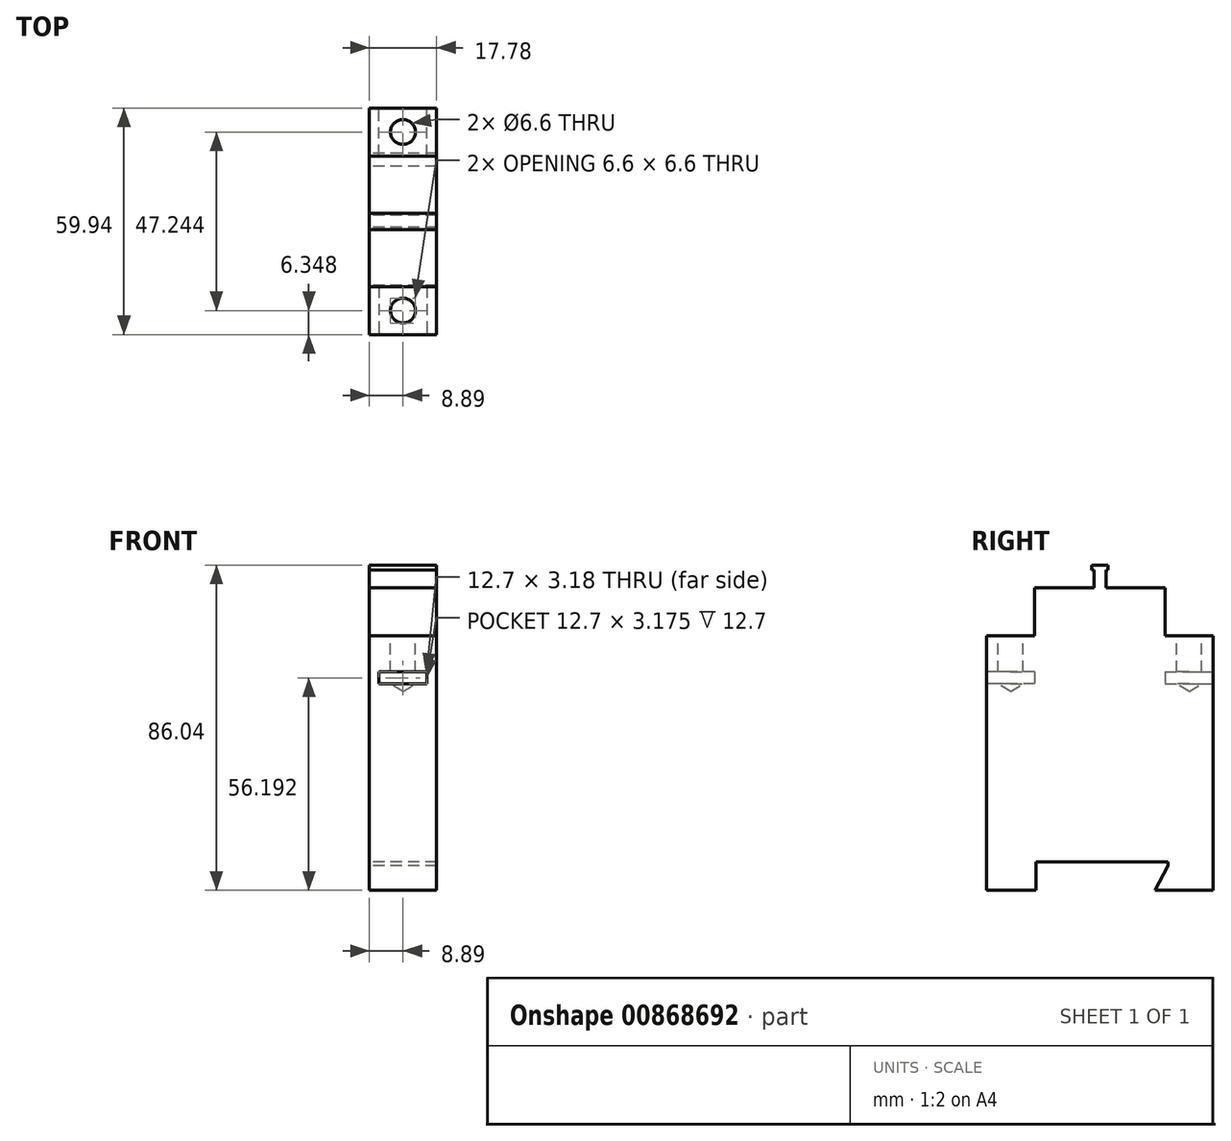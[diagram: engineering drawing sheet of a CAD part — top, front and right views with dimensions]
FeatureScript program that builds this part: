
annotation { "Feature Type Name" : "Feature", "Feature Type Description" : "" }
export const myFeature = defineFeature(function(context is Context, id is Id, definition is map)
    precondition{}
    {
        {
            var Q0;
            Q0=qCreatedBy(makeId("Right.planeOp"),FACE);
            var sketch = newSketch(context, id + "F0", { "sketchPlane" : qUnion([Q0])});
            skLineSegment(sketch, "E0.bottom", {"start": v(-17.8, 40) * mm, "end": v(16.74, 40) * mm});
            skLineSegment(sketch, "E0.top", {"start": v(-30.5, -40) * mm, "end": v(29.44, -40) * mm});
            skLineSegment(sketch, "E0.left", {"start": v(-30.5, 27.3) * mm, "end": v(-30.5, -40) * mm});
            skLineSegment(sketch, "E0.right", {"start": v(29.44, 27.3) * mm, "end": v(29.44, -40) * mm});
            skPoint(sketch, "E0.middle", {"position": v(0, 0) * mm});
            skLineSegment(sketch, "E1", {"start": v(-17.5, -33.5) * mm, "end": v(-17.5, -32.5) * mm});
            skLineSegment(sketch, "E2", {"start": v(-17.5, -32.5) * mm, "end": v(17.5, -32.5) * mm});
            skLineSegment(sketch, "E3", {"start": v(17.5, -32.5) * mm, "end": v(17.5, -33.5) * mm});
            skPoint(sketch, "E4.orphan", {"position": v(-17.5, -40) * mm});
            skLineSegment(sketch, "E5", {"start": v(-17.5, -33.5) * mm, "end": v(-17.5, -40) * mm});
            skLineSegment(sketch, "E6", {"start": v(17.5, -33.5) * mm, "end": v(14, -40) * mm});
            skPoint(sketch, "E7.orphan", {"position": v(17.5, -40) * mm});
            skLineSegment(sketch, "E8", {"start": v(-30.5, 27.3) * mm, "end": v(-17.8, 27.3) * mm});
            skLineSegment(sketch, "E9", {"start": v(-17.8, 27.3) * mm, "end": v(-17.8, 40) * mm});
            skLineSegment(sketch, "E10", {"start": v(16.74, 40) * mm, "end": v(16.74, 27.3) * mm});
            skLineSegment(sketch, "E11", {"start": v(16.74, 27.3) * mm, "end": v(29.44, 27.3) * mm});
            skArc(sketch, "E12", {"start": v(10.4, 40) * mm, "mid": v(-0.53, 42.37) * mm, "end": v(-11.45, 40) * mm});
            skLineSegment(sketch, "E13", {"start": v(-0.53, 40) * mm, "end": v(-0.53, 38.72) * mm});
            skLineSegment(sketch, "E14.bottom", {"start": v(-2.12, 40) * mm, "end": v(1.06, 40) * mm});
            skLineSegment(sketch, "E14.top", {"start": v(-2.12, 45.09) * mm, "end": v(1.06, 45.09) * mm});
            skLineSegment(sketch, "E14.left", {"start": v(-2.12, 40) * mm, "end": v(-2.12, 45.09) * mm});
            skLineSegment(sketch, "E14.right", {"start": v(1.06, 40) * mm, "end": v(1.06, 45.09) * mm});
            skLineSegment(sketch, "E15.bottom", {"start": v(-2.75, 46.04) * mm, "end": v(1.63, 46.04) * mm});
            skLineSegment(sketch, "E15.top", {"start": v(-2.75, 44.77) * mm, "end": v(1.63, 44.77) * mm});
            skLineSegment(sketch, "E15.left", {"start": v(-2.75, 46.04) * mm, "end": v(-2.75, 44.77) * mm});
            skLineSegment(sketch, "E15.right", {"start": v(1.63, 46.04) * mm, "end": v(1.63, 44.77) * mm});
            skSolve(sketch);
        }
        {
            var Q0;
            Q0=makeQuery(id+"F0.imprint","IMPRINT",FACE,{"disambiguationData":[TD([[makeQuery(id+"F0.imprint","IMPRINT",EDGE,{"derivedFrom":sQuery(id+"F0.wireOp",EDGE,"E0.bottom")}),-1.0]])]});
            extrude(context, id + "F1", {"entities" : qUnion([Q0]), "depth" : 17.78 * mm, "offsetDistance" : 25.4 * mm});
        }
        {
            var Q0;
            {var subQ0=sQuery(id+"F0.wireOp",EDGE,"E12");var subQ1=sQuery(id+"F0.wireOp",EDGE,"E0.bottom");var subQ2=makeQuery(id+"F0.imprint","INTERSECT",VERTEX,{"disambiguationData":[OD(1.0)],"derivedFrom":[subQ1,subQ0]});Q0=makeQuery(id+"F0.imprint","IMPRINT",FACE,{"disambiguationData":[TD([[makeQuery(id+"F0.imprint","IMPRINT",EDGE,{"disambiguationData":[TD([[subQ2,1.0]])],"derivedFrom":subQ0}),1.0]])]});}
            var Q1;
            {var subQ2=sQuery(id+"F0.wireOp",EDGE,"E14.right");var subQ7=sQuery(id+"F0.wireOp",EDGE,"E12");var subQ9=makeQuery(id+"F0.imprint","INTERSECT",VERTEX,{"derivedFrom":[subQ7,subQ2]});Q1=makeQuery(id+"F0.imprint","IMPRINT",FACE,{"disambiguationData":[TD([[makeQuery(id+"F0.imprint","IMPRINT",EDGE,{"disambiguationData":[TD([[subQ9,-1.0]])],"derivedFrom":subQ7}),1.0]])]});}
            var Q2;
            {var subQ0=sQuery(id+"F0.wireOp",EDGE,"E12");var subQ1=sQuery(id+"F0.wireOp",EDGE,"E0.bottom");var subQ2=makeQuery(id+"F0.imprint","INTERSECT",VERTEX,{"disambiguationData":[OD(0.0)],"derivedFrom":[subQ1,subQ0]});Q2=makeQuery(id+"F0.imprint","IMPRINT",FACE,{"disambiguationData":[TD([[makeQuery(id+"F0.imprint","IMPRINT",EDGE,{"disambiguationData":[TD([[subQ2,-1.0]])],"derivedFrom":subQ0}),1.0]])]});}
            var Q3;
            {var subQ0=sQuery(id+"F0.wireOp",EDGE,"E14.right");var subQ1=sQuery(id+"F0.wireOp",EDGE,"E12");var subQ2=makeQuery(id+"F0.imprint","INTERSECT",VERTEX,{"derivedFrom":[subQ1,subQ0]});Q3=makeQuery(id+"F0.imprint","IMPRINT",FACE,{"disambiguationData":[TD([[makeQuery(id+"F0.imprint","IMPRINT",EDGE,{"disambiguationData":[TD([[subQ2,-1.0]])],"derivedFrom":subQ1}),-1.0]])]});}
            var Q4;
            {var subQ0=sQuery(id+"F0.wireOp",EDGE,"E14.top");Q4=makeQuery(id+"F0.imprint","IMPRINT",FACE,{"disambiguationData":[TD([[makeQuery(id+"F0.imprint","IMPRINT",EDGE,{"derivedFrom":subQ0}),-1.0]])]});}
            var Q5;
            {var subQ1=sQuery(id+"F0.wireOp",EDGE,"E14.top");Q5=makeQuery(id+"F0.imprint","IMPRINT",FACE,{"disambiguationData":[TD([[makeQuery(id+"F0.imprint","IMPRINT",EDGE,{"derivedFrom":subQ1}),1.0]])]});}
            var Q6;
            Q6=makeQuery(id+"F1.opExtrude","CAP_FACE",FACE,{"disambiguationData":[OSD([sQuery(id+"F0.wireOp",EDGE,"E0.bottom"),sQuery(id+"F0.wireOp",EDGE,"E0.top"),sQuery(id+"F0.wireOp",EDGE,"E0.left"),sQuery(id+"F0.wireOp",EDGE,"E0.right"),sQuery(id+"F0.wireOp",EDGE,"E1"),sQuery(id+"F0.wireOp",EDGE,"E2"),sQuery(id+"F0.wireOp",EDGE,"E3"),sQuery(id+"F0.wireOp",EDGE,"E5"),sQuery(id+"F0.wireOp",EDGE,"E6"),sQuery(id+"F0.wireOp",EDGE,"E8"),sQuery(id+"F0.wireOp",EDGE,"E9"),sQuery(id+"F0.wireOp",EDGE,"E10"),sQuery(id+"F0.wireOp",EDGE,"E11"),sQuery(id+"F0.wireOp",EDGE,"E14.bottom")])],"isStart":false});
            extrude(context, id + "F2", {"entities" : qUnion([Q0, Q1, Q2, Q3, Q4, Q5]), "operationType" : NewBodyOperationType.ADD, "endBound" : BoundingType.UP_TO_SURFACE, "depth" : 25.4 * mm, "endBoundEntityFace" : qUnion([Q6]), "offsetDistance" : 25.4 * mm});
        }
        {
            var Q0;
            Q0=makeQuery(id+"F1.opExtrude","SWEPT_FACE",FACE,{"disambiguationData":[OSD([sQuery(id+"F0.wireOp",EDGE,"E8")])]});
            var sketch = newSketch(context, id + "F3", { "sketchPlane" : qUnion([Q0])});
            skPoint(sketch, "E16", {"position": v(8.9, -24.15) * mm});
            skPoint(sketch, "E16.positionSnap0", {"position": v(8.9, -17.8) * mm});
            skPoint(sketch, "E16.positionSnap1", {"position": v(0, -24.15) * mm});
            skSolve(sketch);
        }
        {
            var Q0;
            Q0=makeQuery(id+"F1.opExtrude","SWEPT_FACE",FACE,{"disambiguationData":[OSD([sQuery(id+"F0.wireOp",EDGE,"E11")])]});
            var sketch = newSketch(context, id + "F4", { "sketchPlane" : qUnion([Q0])});
            skPoint(sketch, "E17", {"position": v(8.9, 23.1) * mm});
            skPoint(sketch, "E17.positionSnap0", {"position": v(8.9, 29.44) * mm});
            skPoint(sketch, "E17.positionSnap1", {"position": v(0, 23.1) * mm});
            skSolve(sketch);
        }
        {
            var Q0;
            Q0=sQuery(id+"F4.wireOp",VERTEX,"E17");
            var Q1;
            Q1=sQuery(id+"F3.wireOp",VERTEX,"E16");
            var Q2;
            Q2=makeQuery(id+"F1.opExtrude","SWEPT_BODY",BODY,{"disambiguationData":[OSD([sQuery(id+"F0.wireOp",EDGE,"E0.bottom"),sQuery(id+"F0.wireOp",EDGE,"E0.top"),sQuery(id+"F0.wireOp",EDGE,"E0.left"),sQuery(id+"F0.wireOp",EDGE,"E0.right"),sQuery(id+"F0.wireOp",EDGE,"E1"),sQuery(id+"F0.wireOp",EDGE,"E2"),sQuery(id+"F0.wireOp",EDGE,"E3"),sQuery(id+"F0.wireOp",EDGE,"E5"),sQuery(id+"F0.wireOp",EDGE,"E6"),sQuery(id+"F0.wireOp",EDGE,"E8"),sQuery(id+"F0.wireOp",EDGE,"E9"),sQuery(id+"F0.wireOp",EDGE,"E10"),sQuery(id+"F0.wireOp",EDGE,"E11"),sQuery(id+"F0.wireOp",EDGE,"E14.bottom")])]});
            hole(context, id + "F5", {"style" : HoleStyle.SIMPLE, "endStyle" : HoleEndStyle.BLIND, "standardTappedOrClearance" : lookupTablePath({ "fit" : "Normal", "standard" : "ISO", "size" : "M6", "type" : "Clearance" }), "standardBlindInLast" : lookupTablePath({ "fit" : "Normal", "standard" : "ISO", "size" : "M6", "type" : "Clearance" }), "holeDiameter" : 6.6 * mm, "majorDiameter" : 2.84 * mm, "holeDepth" : 12.7 * mm, "isTappedThrough" : true, "tappedDepth" : 12.7 * mm, "tapClearance" : 3, "locations" : qUnion([Q0, Q1]), "scope" : qUnion([Q2])});
        }
        {
            var Q0;
            Q0=makeQuery(id+"F1.opExtrude","SWEPT_FACE",FACE,{"disambiguationData":[OSD([sQuery(id+"F0.wireOp",EDGE,"E0.left")])]});
            var sketch = newSketch(context, id + "F6", { "sketchPlane" : qUnion([Q0])});
            skLineSegment(sketch, "E18.bottom", {"start": v(2.54, 17.78) * mm, "end": v(15.24, 17.78) * mm});
            skLineSegment(sketch, "E18.top", {"start": v(2.54, 14.6) * mm, "end": v(15.24, 14.6) * mm});
            skLineSegment(sketch, "E18.left", {"start": v(2.54, 17.78) * mm, "end": v(2.54, 14.6) * mm});
            skLineSegment(sketch, "E18.right", {"start": v(15.24, 17.78) * mm, "end": v(15.24, 14.6) * mm});
            skPoint(sketch, "E18.middle", {"position": v(8.9, 16.2) * mm});
            skPoint(sketch, "E18.middle.positionSnap0", {"position": v(8.9, 27.3) * mm});
            skPoint(sketch, "E18.centerSnap0", {"position": v(8.9, 27.3) * mm});
            skSolve(sketch);
        }
        {
            var Q0;
            Q0=makeQuery(id+"F1.opExtrude","SWEPT_FACE",FACE,{"disambiguationData":[OSD([sQuery(id+"F0.wireOp",EDGE,"E0.right")])]});
            var sketch = newSketch(context, id + "F7", { "sketchPlane" : qUnion([Q0])});
            skLineSegment(sketch, "E19.bottom", {"start": v(-15.24, 17.78) * mm, "end": v(-2.54, 17.78) * mm});
            skLineSegment(sketch, "E19.top", {"start": v(-15.24, 14.6) * mm, "end": v(-2.54, 14.6) * mm});
            skLineSegment(sketch, "E19.left", {"start": v(-15.24, 17.78) * mm, "end": v(-15.24, 14.6) * mm});
            skLineSegment(sketch, "E19.right", {"start": v(-2.54, 17.78) * mm, "end": v(-2.54, 14.6) * mm});
            skPoint(sketch, "E19.middle", {"position": v(-8.9, 16.2) * mm});
            skPoint(sketch, "E19.middle.positionSnap0", {"position": v(-8.9, 27.3) * mm});
            skPoint(sketch, "E19.centerSnap0", {"position": v(-8.9, 27.3) * mm});
            skSolve(sketch);
        }
        {
            var Q0;
            Q0=makeQuery(id+"F6.imprint","IMPRINT",FACE,{"disambiguationData":[TD([[makeQuery(id+"F6.imprint","IMPRINT",EDGE,{"derivedFrom":sQuery(id+"F6.wireOp",EDGE,"E18.bottom")}),-1.0]])]});
            extrude(context, id + "F8", {"entities" : qUnion([Q0]), "operationType" : NewBodyOperationType.REMOVE, "oppositeDirection" : true, "depth" : 12.7 * mm, "offsetDistance" : 25.4 * mm});
        }
        {
            var Q0;
            Q0=makeQuery(id+"F7.imprint","IMPRINT",FACE,{"disambiguationData":[TD([[makeQuery(id+"F7.imprint","IMPRINT",EDGE,{"derivedFrom":sQuery(id+"F7.wireOp",EDGE,"E19.bottom")}),-1.0]])]});
            extrude(context, id + "F9", {"entities" : qUnion([Q0]), "operationType" : NewBodyOperationType.REMOVE, "oppositeDirection" : true, "depth" : 12.7 * mm, "offsetDistance" : 25.4 * mm});
        }
    });
